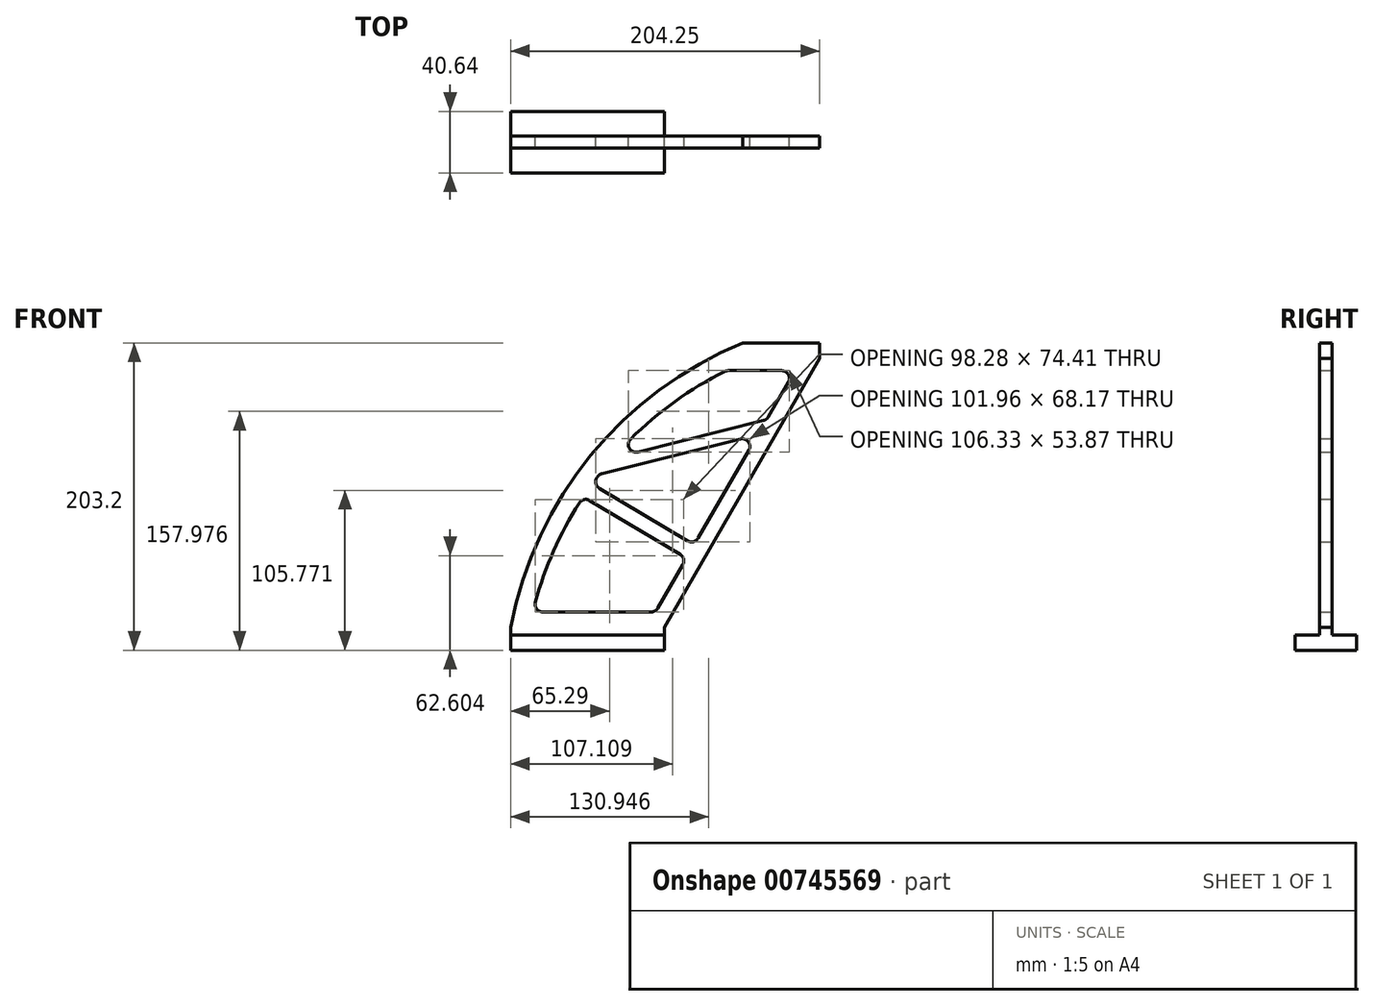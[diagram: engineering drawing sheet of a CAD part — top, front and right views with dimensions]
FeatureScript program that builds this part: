
annotation { "Feature Type Name" : "Feature", "Feature Type Description" : "" }
export const myFeature = defineFeature(function(context is Context, id is Id, definition is map)
    precondition{}
    {
        {
            var Q0;
            Q0=qCreatedBy(makeId("Front.planeOp"),FACE);
            var sketch = newSketch(context, id + "F0", { "sketchPlane" : qUnion([Q0])});
            skLineSegment(sketch, "E0", {"start": v(0, 15.24) * mm, "end": v(0, 0) * mm});
            skLineSegment(sketch, "E1", {"start": v(0, 0) * mm, "end": v(101.6, 0) * mm});
            skLineSegment(sketch, "E2", {"start": v(101.6, 0) * mm, "end": v(101.6, 15.24) * mm});
            skLineSegment(sketch, "E3", {"start": v(101.6, 15.24) * mm, "end": v(204.25, 193.04) * mm});
            skLineSegment(sketch, "E4", {"start": v(204.25, 193.04) * mm, "end": v(204.25, 203.2) * mm});
            skLineSegment(sketch, "E5", {"start": v(204.25, 203.2) * mm, "end": v(153.45, 203.2) * mm});
            skArc(sketch, "E6", {"start": v(153.45, 203.2) * mm, "mid": v(52.83, 128.73) * mm, "end": v(0, 15.24) * mm});
            skLineSegment(sketch, "E7", {"start": v(21.23, 25.4) * mm, "end": v(92.8, 25.4) * mm});
            skLineSegment(sketch, "E8", {"start": v(97.2, 27.94) * mm, "end": v(113.76, 56.62) * mm});
            skLineSegment(sketch, "E9", {"start": v(179.03, 184.91) * mm, "end": v(143.72, 184.91) * mm});
            skArc(sketch, "E10", {"start": v(141.45, 184.38) * mm, "mid": v(108.56, 164.52) * mm, "end": v(79.23, 139.7) * mm});
            skLineSegment(sketch, "E11", {"start": v(166.97, 151.88) * mm, "end": v(84.04, 131.17) * mm});
            skLineSegment(sketch, "E12", {"start": v(52.18, 99.1) * mm, "end": v(111.96, 63.52) * mm});
            skLineSegment(sketch, "E13", {"start": v(151.79, 139.71) * mm, "end": v(60.35, 116.88) * mm});
            skLineSegment(sketch, "E14", {"start": v(58.6, 107.1) * mm, "end": v(116.92, 72.4) * mm});
            skLineSegment(sketch, "E15", {"start": v(0, 10.16) * mm, "end": v(101.6, 10.16) * mm});
            skLineSegment(sketch, "E16.trimOffspring", {"start": v(170.14, 154.27) * mm, "end": v(183.43, 177.3) * mm});
            skLineSegment(sketch, "E17.trimOffspring", {"start": v(123.92, 74.22) * mm, "end": v(157.42, 132.24) * mm});
            skArc(sketch, "E18.trimOffspring", {"start": v(57.55, 115.04) * mm, "mid": v(57.36, 114.79) * mm, "end": v(57.16, 114.54) * mm});
            skArc(sketch, "E19.trimOffspring", {"start": v(45.29, 97.45) * mm, "mid": v(28.36, 65.71) * mm, "end": v(16.33, 31.82) * mm});
            skPoint(sketch, "E20.visualSharp", {"position": v(53.77, 109.97) * mm});
            skArc(sketch, "E20.filletArc", {"start": v(57.16, 114.54) * mm, "mid": v(56.22, 110.5) * mm, "end": v(58.6, 107.1) * mm});
            skPoint(sketch, "E21.visualSharp", {"position": v(58.64, 116.45) * mm});
            skArc(sketch, "E21.filletArc", {"start": v(60.35, 116.88) * mm, "mid": v(58.8, 116.2) * mm, "end": v(57.55, 115.04) * mm});
            skPoint(sketch, "E22.visualSharp", {"position": v(163.4, 142.61) * mm});
            skArc(sketch, "E22.filletArc", {"start": v(157.42, 132.24) * mm, "mid": v(157.08, 137.84) * mm, "end": v(151.79, 139.71) * mm});
            skPoint(sketch, "E23.visualSharp", {"position": v(169.06, 152.4) * mm});
            skArc(sketch, "E23.filletArc", {"start": v(166.97, 151.88) * mm, "mid": v(168.8, 152.75) * mm, "end": v(170.14, 154.27) * mm});
            skPoint(sketch, "E24.visualSharp", {"position": v(187.83, 184.91) * mm});
            skArc(sketch, "E24.filletArc", {"start": v(183.43, 177.3) * mm, "mid": v(183.43, 182.37) * mm, "end": v(179.03, 184.91) * mm});
            skPoint(sketch, "E25.visualSharp", {"position": v(142.53, 184.91) * mm});
            skArc(sketch, "E25.filletArc", {"start": v(143.72, 184.91) * mm, "mid": v(142.55, 184.78) * mm, "end": v(141.45, 184.38) * mm});
            skPoint(sketch, "E26.visualSharp", {"position": v(67.32, 127) * mm});
            skArc(sketch, "E26.filletArc", {"start": v(79.23, 139.7) * mm, "mid": v(78.39, 133.6) * mm, "end": v(84.04, 131.17) * mm});
            skPoint(sketch, "E27.visualSharp", {"position": v(121.35, 69.76) * mm});
            skArc(sketch, "E27.filletArc", {"start": v(116.92, 72.4) * mm, "mid": v(120.8, 71.84) * mm, "end": v(123.92, 74.22) * mm});
            skPoint(sketch, "E28.visualSharp", {"position": v(116.26, 60.96) * mm});
            skArc(sketch, "E28.filletArc", {"start": v(113.76, 56.62) * mm, "mid": v(114.27, 60.44) * mm, "end": v(111.96, 63.52) * mm});
            skPoint(sketch, "E29.visualSharp", {"position": v(95.73, 25.4) * mm});
            skArc(sketch, "E29.filletArc", {"start": v(92.8, 25.4) * mm, "mid": v(95.34, 26.08) * mm, "end": v(97.2, 27.94) * mm});
            skPoint(sketch, "E30.visualSharp", {"position": v(14.67, 25.4) * mm});
            skArc(sketch, "E30.filletArc", {"start": v(16.33, 31.82) * mm, "mid": v(17.19, 27.4) * mm, "end": v(21.23, 25.4) * mm});
            skPoint(sketch, "E31.visualSharp", {"position": v(47.97, 101.6) * mm});
            skArc(sketch, "E31.filletArc", {"start": v(52.18, 99.1) * mm, "mid": v(48.4, 99.67) * mm, "end": v(45.29, 97.45) * mm});
            skSolve(sketch);
        }
        {
            var Q0;
            {var subQ1=sQuery(id+"F0.wireOp",EDGE,"E3");Q0=makeQuery(id+"F0.imprint","IMPRINT",FACE,{"disambiguationData":[TD([[makeQuery(id+"F0.imprint","IMPRINT",EDGE,{"derivedFrom":subQ1}),1.0]])]});}
            extrude(context, id + "F1", {"entities" : qUnion([Q0]), "endBound" : BoundingType.SYMMETRIC, "depth" : 8.13 * mm, "offsetDistance" : 25.4 * mm});
        }
        {
            var Q0;
            {var subQ0=sQuery(id+"F0.wireOp",EDGE,"E1");Q0=makeQuery(id+"F0.imprint","IMPRINT",FACE,{"disambiguationData":[TD([[makeQuery(id+"F0.imprint","IMPRINT",EDGE,{"derivedFrom":subQ0}),1.0]])]});}
            extrude(context, id + "F2", {"entities" : qUnion([Q0]), "operationType" : NewBodyOperationType.ADD, "endBound" : BoundingType.SYMMETRIC, "depth" : 40.64 * mm, "offsetDistance" : 25.4 * mm});
        }
    });
